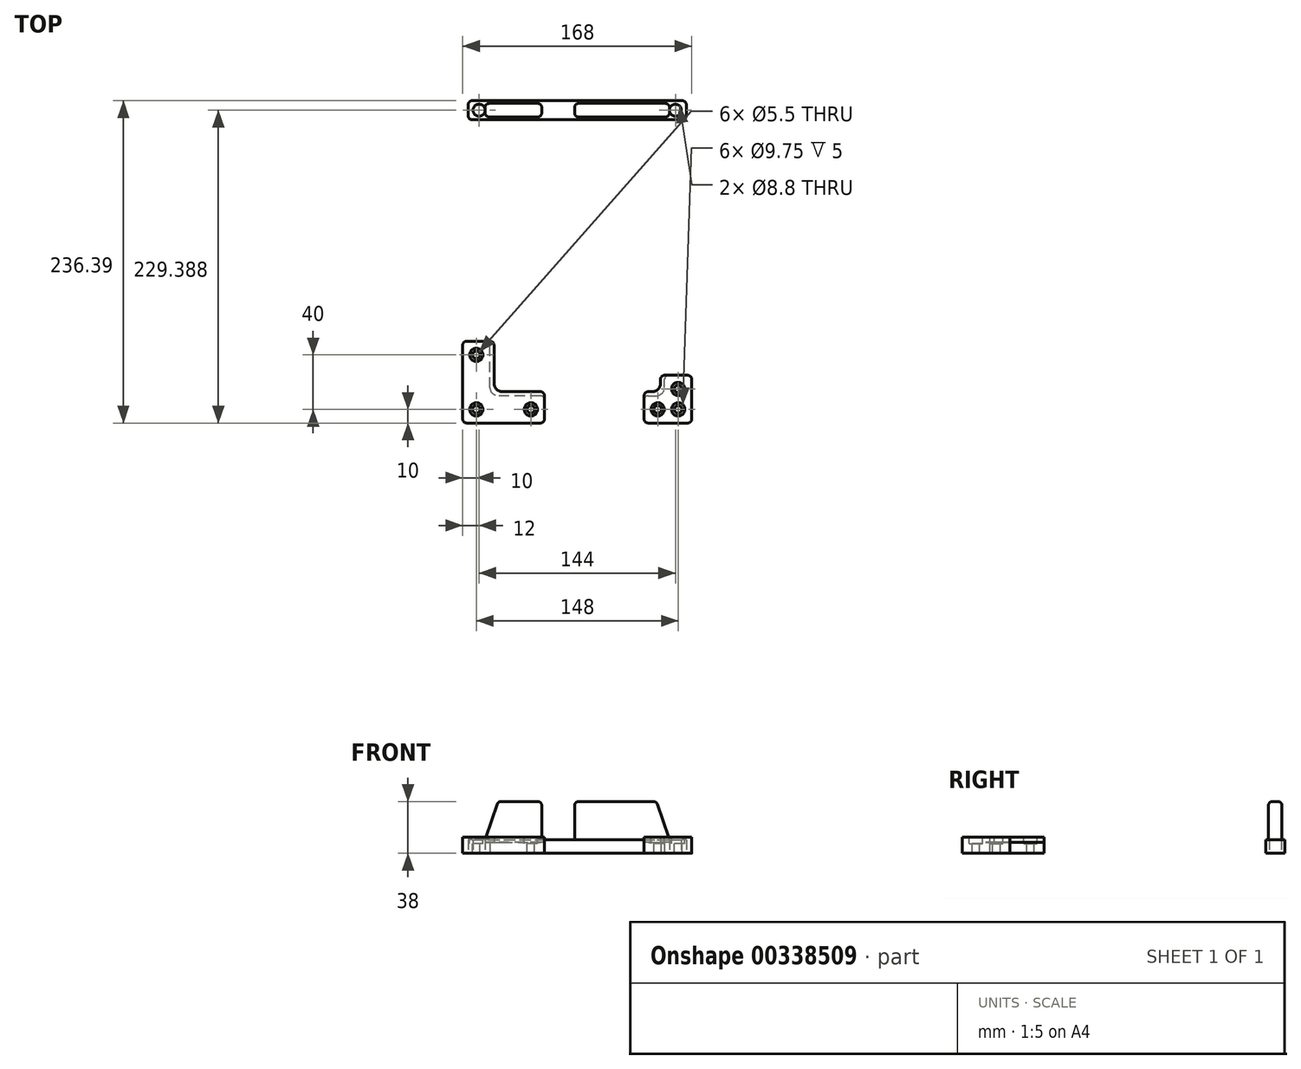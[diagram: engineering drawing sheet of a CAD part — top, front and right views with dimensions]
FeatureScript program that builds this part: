
annotation { "Feature Type Name" : "Feature", "Feature Type Description" : "" }
export const myFeature = defineFeature(function(context is Context, id is Id, definition is map)
    precondition{}
    {
        {
            var Q0;
            Q0=qCreatedBy(makeId("Top.planeOp"),FACE);
            var sketch = newSketch(context, id + "F0", { "sketchPlane" : qUnion([Q0])});
            skLineSegment(sketch, "E0.bottom", {"start": v(64, 114) * mm, "end": v(-64, 114) * mm, "construction": true});
            skLineSegment(sketch, "E0.top", {"start": v(64, -114) * mm, "end": v(-64, -114) * mm, "construction": true});
            skLineSegment(sketch, "E0.left", {"start": v(64, 114) * mm, "end": v(64, -114) * mm, "construction": true});
            skLineSegment(sketch, "E0.right", {"start": v(-64, 114) * mm, "end": v(-64, -114) * mm, "construction": true});
            skPoint(sketch, "E0.middle", {"position": v(0, 0) * mm});
            skLineSegment(sketch, "E1.bottom", {"start": v(88.4, -74) * mm, "end": v(-88.4, -74) * mm, "construction": true});
            skLineSegment(sketch, "E1.top", {"start": v(88.4, 9) * mm, "end": v(-88.4, 9) * mm, "construction": true});
            skLineSegment(sketch, "E1.left", {"start": v(88.4, -74) * mm, "end": v(88.4, 9) * mm, "construction": true});
            skLineSegment(sketch, "E1.right", {"start": v(-88.4, -74) * mm, "end": v(-88.4, 9) * mm, "construction": true});
            skPoint(sketch, "E1.middle", {"position": v(0, -32.5) * mm});
            skLineSegment(sketch, "E2", {"start": v(-64, -114) * mm, "end": v(-64, -74) * mm});
            skLineSegment(sketch, "E3", {"start": v(-64, -74) * mm, "end": v(-84, -74) * mm});
            skLineSegment(sketch, "E4", {"start": v(-84, -74) * mm, "end": v(-84, -134) * mm});
            skLineSegment(sketch, "E5", {"start": v(-84, -134) * mm, "end": v(-24, -134) * mm});
            skLineSegment(sketch, "E6", {"start": v(-24, -134) * mm, "end": v(-24, -114) * mm});
            skLineSegment(sketch, "E7", {"start": v(-24, -114) * mm, "end": v(-64, -114) * mm});
            skLineSegment(sketch, "E8", {"start": v(64, -114) * mm, "end": v(64, -99) * mm});
            skLineSegment(sketch, "E9", {"start": v(64, -99) * mm, "end": v(84, -99) * mm});
            skLineSegment(sketch, "E10", {"start": v(84, -99) * mm, "end": v(84, -134) * mm});
            skLineSegment(sketch, "E11", {"start": v(84, -134) * mm, "end": v(49, -134) * mm});
            skLineSegment(sketch, "E12", {"start": v(49, -134) * mm, "end": v(49, -114) * mm});
            skLineSegment(sketch, "E13", {"start": v(49, -114) * mm, "end": v(64, -114) * mm});
            skLineSegment(sketch, "E14.bottom", {"start": v(-80, 102.39) * mm, "end": v(80, 102.39) * mm});
            skLineSegment(sketch, "E14.top", {"start": v(-80, 88.39) * mm, "end": v(80, 88.39) * mm});
            skLineSegment(sketch, "E14.left", {"start": v(-80, 102.39) * mm, "end": v(-80, 88.39) * mm});
            skLineSegment(sketch, "E14.right", {"start": v(80, 102.39) * mm, "end": v(80, 88.39) * mm});
            skLineSegment(sketch, "E15", {"start": v(-80, 95.39) * mm, "end": v(-72, 95.39) * mm, "construction": true});
            skLineSegment(sketch, "E16", {"start": v(80, 95.39) * mm, "end": v(72, 95.39) * mm, "construction": true});
            skSolve(sketch);
        }
        {
            var Q0;
            Q0=makeQuery(id+"F0.imprint","IMPRINT",FACE,{"disambiguationData":[TD([[makeQuery(id+"F0.imprint","IMPRINT",EDGE,{"derivedFrom":sQuery(id+"F0.wireOp",EDGE,"E2")}),1.0]])]});
            var Q1;
            Q1=makeQuery(id+"F0.imprint","IMPRINT",FACE,{"disambiguationData":[TD([[makeQuery(id+"F0.imprint","IMPRINT",EDGE,{"derivedFrom":sQuery(id+"F0.wireOp",EDGE,"E8")}),-1.0]])]});
            extrude(context, id + "F1", {"entities" : qUnion([Q0, Q1]), "depth" : 8 * mm});
        }
        {
            assignVariable(context, id + "F2", {"name" : "offset", "anyValue" : 3});
        }
        {
            var Q0;
            Q0=makeQuery(id+"F1.opExtrude","CAP_FACE",FACE,{"disambiguationData":[OSD([sQuery(id+"F0.wireOp",EDGE,"E2"),sQuery(id+"F0.wireOp",EDGE,"E3"),sQuery(id+"F0.wireOp",EDGE,"E4"),sQuery(id+"F0.wireOp",EDGE,"E5"),sQuery(id+"F0.wireOp",EDGE,"E6"),sQuery(id+"F0.wireOp",EDGE,"E7")])],"isStart":false});
            var sketch = newSketch(context, id + "F3", { "sketchPlane" : qUnion([Q0])});
            skLineSegment(sketch, "E17", {"start": v(-84, -74) * mm, "end": v(-61, -74) * mm});
            skLineSegment(sketch, "E18", {"start": v(-61, -74) * mm, "end": v(-61, -111) * mm});
            skLineSegment(sketch, "E19", {"start": v(-61, -111) * mm, "end": v(-24, -111) * mm});
            skLineSegment(sketch, "E20", {"start": v(-24, -111) * mm, "end": v(-24, -134) * mm});
            skLineSegment(sketch, "E21", {"start": v(-24, -134) * mm, "end": v(-84, -134) * mm});
            skLineSegment(sketch, "E22", {"start": v(-84, -134) * mm, "end": v(-84, -74) * mm});
            skPoint(sketch, "E23.0", {"position": v(49, -134) * mm});
            skPoint(sketch, "E23.1", {"position": v(84, -134) * mm});
            skPoint(sketch, "E23.2", {"position": v(84, -99) * mm});
            skLineSegment(sketch, "E24", {"start": v(49, -134) * mm, "end": v(84, -134) * mm});
            skLineSegment(sketch, "E25", {"start": v(84, -99) * mm, "end": v(61, -99) * mm});
            skLineSegment(sketch, "E26", {"start": v(61, -99) * mm, "end": v(61, -111) * mm});
            skLineSegment(sketch, "E27", {"start": v(61, -111) * mm, "end": v(49, -111) * mm});
            skLineSegment(sketch, "E28", {"start": v(49, -111) * mm, "end": v(49, -134) * mm});
            skLineSegment(sketch, "E29", {"start": v(84, -134) * mm, "end": v(84, -99) * mm});
            skSolve(sketch);
        }
        {
            var Q0;
            {var subQ4=sQuery(id+"F3.wireOp",EDGE,"E18");Q0=makeQuery(id+"F3.imprint","IMPRINT",FACE,{"disambiguationData":[TD([[makeQuery(id+"F3.imprint","IMPRINT",EDGE,{"derivedFrom":subQ4}),-1.0]])]});}
            var Q1;
            {var subQ1=sQuery(id+"F3.wireOp",EDGE,"E21");Q1=makeQuery(id+"F3.imprint","IMPRINT",FACE,{"disambiguationData":[TD([[makeQuery(id+"F3.imprint","IMPRINT",EDGE,{"derivedFrom":subQ1}),1.0]])]});}
            var Q2;
            Q2=makeQuery(id+"F3.imprint","IMPRINT",FACE,{"disambiguationData":[TD([[makeQuery(id+"F3.imprint","IMPRINT",EDGE,{"derivedFrom":sQuery(id+"F3.wireOp",EDGE,"E24")}),1.0]])]});
            extrude(context, id + "F4", {"entities" : qUnion([Q0, Q1, Q2]), "operationType" : NewBodyOperationType.ADD, "depth" : 4 * mm});
        }
        {
            var Q0;
            Q0=makeQuery(id+"F4.boolean.opBoolean","MERGE",EDGE,{"derivedFrom":[makeQuery(id+"F1.opExtrude","SWEPT_EDGE",EDGE,{"disambiguationData":[OSD([sQuery(id+"F0.wireOp",EDGE,"E4"),sQuery(id+"F0.wireOp",EDGE,"E5")])]}),makeQuery(id+"F4.opExtrude","SWEPT_EDGE",EDGE,{"disambiguationData":[OSD([sQuery(id+"F3.wireOp",EDGE,"E21"),sQuery(id+"F3.wireOp",EDGE,"E22")])]})]});
            var Q1;
            Q1=makeQuery(id+"F4.boolean.opBoolean","MERGE",EDGE,{"derivedFrom":[makeQuery(id+"F1.opExtrude","SWEPT_EDGE",EDGE,{"disambiguationData":[OSD([sQuery(id+"F0.wireOp",EDGE,"E5"),sQuery(id+"F0.wireOp",EDGE,"E6")])]}),makeQuery(id+"F4.opExtrude","SWEPT_EDGE",EDGE,{"disambiguationData":[OSD([sQuery(id+"F3.wireOp",EDGE,"E20"),sQuery(id+"F3.wireOp",EDGE,"E21")])]})]});
            var Q2;
            Q2=makeQuery(id+"F4.boolean.opBoolean","MERGE",EDGE,{"derivedFrom":[makeQuery(id+"F1.opExtrude","SWEPT_EDGE",EDGE,{"disambiguationData":[OSD([sQuery(id+"F0.wireOp",EDGE,"E3"),sQuery(id+"F0.wireOp",EDGE,"E4")])]}),makeQuery(id+"F4.opExtrude","SWEPT_EDGE",EDGE,{"disambiguationData":[OSD([sQuery(id+"F3.wireOp",EDGE,"E17"),sQuery(id+"F3.wireOp",EDGE,"E22")])]})]});
            var Q3;
            Q3=makeQuery(id+"F4.boolean.opBoolean","MERGE",EDGE,{"derivedFrom":[makeQuery(id+"F1.opExtrude","SWEPT_EDGE",EDGE,{"disambiguationData":[OSD([sQuery(id+"F0.wireOp",EDGE,"E11"),sQuery(id+"F0.wireOp",EDGE,"E12")])]}),makeQuery(id+"F4.opExtrude","SWEPT_EDGE",EDGE,{"disambiguationData":[OSD([sQuery(id+"F3.wireOp",EDGE,"E24"),sQuery(id+"F3.wireOp",EDGE,"E28")])]})]});
            var Q4;
            Q4=makeQuery(id+"F4.boolean.opBoolean","MERGE",EDGE,{"derivedFrom":[makeQuery(id+"F1.opExtrude","SWEPT_EDGE",EDGE,{"disambiguationData":[OSD([sQuery(id+"F0.wireOp",EDGE,"E10"),sQuery(id+"F0.wireOp",EDGE,"E11")])]}),makeQuery(id+"F4.opExtrude","SWEPT_EDGE",EDGE,{"disambiguationData":[OSD([sQuery(id+"F3.wireOp",EDGE,"E24"),sQuery(id+"F3.wireOp",EDGE,"E29")])]})]});
            var Q5;
            Q5=makeQuery(id+"F4.boolean.opBoolean","MERGE",EDGE,{"derivedFrom":[makeQuery(id+"F1.opExtrude","SWEPT_EDGE",EDGE,{"disambiguationData":[OSD([sQuery(id+"F0.wireOp",EDGE,"E9"),sQuery(id+"F0.wireOp",EDGE,"E10")])]}),makeQuery(id+"F4.opExtrude","SWEPT_EDGE",EDGE,{"disambiguationData":[OSD([sQuery(id+"F3.wireOp",EDGE,"E25"),sQuery(id+"F3.wireOp",EDGE,"E29")])]})]});
            var Q6;
            Q6=makeQuery(id+"F1.opExtrude","SWEPT_EDGE",EDGE,{"disambiguationData":[OSD([sQuery(id+"F0.wireOp",EDGE,"E12"),sQuery(id+"F0.wireOp",EDGE,"E13")])]});
            var Q7;
            Q7=makeQuery(id+"F1.opExtrude","SWEPT_EDGE",EDGE,{"disambiguationData":[OSD([sQuery(id+"F0.wireOp",EDGE,"E8"),sQuery(id+"F0.wireOp",EDGE,"E9")])]});
            var Q8;
            Q8=makeQuery(id+"F1.opExtrude","SWEPT_EDGE",EDGE,{"disambiguationData":[OSD([sQuery(id+"F0.wireOp",EDGE,"E2"),sQuery(id+"F0.wireOp",EDGE,"E3")])]});
            var Q9;
            Q9=makeQuery(id+"F1.opExtrude","SWEPT_EDGE",EDGE,{"disambiguationData":[OSD([sQuery(id+"F0.wireOp",EDGE,"E6"),sQuery(id+"F0.wireOp",EDGE,"E7")])]});
            var Q10;
            Q10=makeQuery(id+"F4.opExtrude","SWEPT_EDGE",EDGE,{"disambiguationData":[OSD([sQuery(id+"F3.wireOp",EDGE,"E27"),sQuery(id+"F3.wireOp",EDGE,"E28")])]});
            var Q11;
            Q11=makeQuery(id+"F4.opExtrude","SWEPT_EDGE",EDGE,{"disambiguationData":[OSD([sQuery(id+"F3.wireOp",EDGE,"E25"),sQuery(id+"F3.wireOp",EDGE,"E26")])]});
            var Q12;
            Q12=makeQuery(id+"F4.opExtrude","SWEPT_EDGE",EDGE,{"disambiguationData":[OSD([sQuery(id+"F3.wireOp",EDGE,"E17"),sQuery(id+"F3.wireOp",EDGE,"E18")])]});
            var Q13;
            Q13=makeQuery(id+"F4.opExtrude","SWEPT_EDGE",EDGE,{"disambiguationData":[OSD([sQuery(id+"F3.wireOp",EDGE,"E19"),sQuery(id+"F3.wireOp",EDGE,"E20")])]});
            fillet(context, id + "F5", {"entities" : qUnion([Q0, Q1, Q2, Q3, Q4, Q5, Q6, Q7, Q8, Q9, Q10, Q11, Q12, Q13]), "radius" : (getVariable(context, 'offset')) * mm, "tangentPropagation" : true, "allowEdgeOverflow" : false});
        }
        {
            var Q0;
            Q0=makeQuery(id+"F1.opExtrude","SWEPT_EDGE",EDGE,{"disambiguationData":[OSD([sQuery(id+"F0.wireOp",EDGE,"E8"),sQuery(id+"F0.wireOp",EDGE,"E13")])]});
            var Q1;
            Q1=makeQuery(id+"F4.opExtrude","SWEPT_EDGE",EDGE,{"disambiguationData":[OSD([sQuery(id+"F3.wireOp",EDGE,"E26"),sQuery(id+"F3.wireOp",EDGE,"E27")])]});
            var Q2;
            Q2=makeQuery(id+"F1.opExtrude","SWEPT_EDGE",EDGE,{"disambiguationData":[OSD([sQuery(id+"F0.wireOp",EDGE,"E2"),sQuery(id+"F0.wireOp",EDGE,"E7")])]});
            var Q3;
            Q3=makeQuery(id+"F4.opExtrude","SWEPT_EDGE",EDGE,{"disambiguationData":[OSD([sQuery(id+"F3.wireOp",EDGE,"E18"),sQuery(id+"F3.wireOp",EDGE,"E19")])]});
            fillet(context, id + "F6", {"entities" : qUnion([Q0, Q1, Q2, Q3]), "radius" : 6 * mm, "tangentPropagation" : true, "allowEdgeOverflow" : false});
        }
        {
            var Q0;
            Q0=makeQuery(id+"F4.opExtrude","CAP_FACE",FACE,{"disambiguationData":[OSD([sQuery(id+"F3.wireOp",EDGE,"E17"),sQuery(id+"F3.wireOp",EDGE,"E18"),sQuery(id+"F3.wireOp",EDGE,"E19"),sQuery(id+"F3.wireOp",EDGE,"E20"),sQuery(id+"F3.wireOp",EDGE,"E21"),sQuery(id+"F3.wireOp",EDGE,"E22")])],"isStart":false});
            var sketch = newSketch(context, id + "F7", { "sketchPlane" : qUnion([Q0])});
            skLineSegment(sketch, "E30.0.0", {"start": v(61, -102) * mm, "end": v(61, -105) * mm, "construction": true});
            skArc(sketch, "E30.0.1", {"start": v(61, -105) * mm, "mid": v(59.24, -109.24) * mm, "end": v(55, -111) * mm, "construction": true});
            skLineSegment(sketch, "E30.0.2", {"start": v(55, -111) * mm, "end": v(52, -111) * mm, "construction": true});
            skArc(sketch, "E30.0.3", {"start": v(52, -111) * mm, "mid": v(49.88, -111.88) * mm, "end": v(49, -114) * mm, "construction": true});
            skLineSegment(sketch, "E30.0.4", {"start": v(49, -114) * mm, "end": v(49, -131) * mm, "construction": true});
            skArc(sketch, "E30.0.5", {"start": v(49, -131) * mm, "mid": v(49.88, -133.12) * mm, "end": v(52, -134) * mm, "construction": true});
            skLineSegment(sketch, "E30.0.6", {"start": v(52, -134) * mm, "end": v(81, -134) * mm, "construction": true});
            skArc(sketch, "E30.0.7", {"start": v(81, -134) * mm, "mid": v(83.12, -133.12) * mm, "end": v(84, -131) * mm, "construction": true});
            skLineSegment(sketch, "E30.0.8", {"start": v(84, -131) * mm, "end": v(84, -102) * mm, "construction": true});
            skArc(sketch, "E30.0.9", {"start": v(84, -102) * mm, "mid": v(83.12, -99.88) * mm, "end": v(81, -99) * mm, "construction": true});
            skLineSegment(sketch, "E30.0.10", {"start": v(81, -99) * mm, "end": v(64, -99) * mm, "construction": true});
            skArc(sketch, "E30.0.11", {"start": v(64, -99) * mm, "mid": v(61.88, -99.88) * mm, "end": v(61, -102) * mm, "construction": true});
            skPoint(sketch, "E31.0", {"position": v(-84, -134) * mm});
            skPoint(sketch, "E31.1", {"position": v(-24, -134) * mm});
            skPoint(sketch, "E31.2", {"position": v(49, -134) * mm});
            skPoint(sketch, "E31.3", {"position": v(84, -134) * mm});
            skPoint(sketch, "E31.4", {"position": v(84, -99) * mm});
            skPoint(sketch, "E31.5", {"position": v(-84, -74) * mm});
            skLineSegment(sketch, "E32", {"start": v(-84, -74) * mm, "end": v(-74, -74) * mm, "construction": true});
            skLineSegment(sketch, "E33", {"start": v(-74, -74) * mm, "end": v(-74, -124) * mm, "construction": true});
            skLineSegment(sketch, "E34", {"start": v(-74, -124) * mm, "end": v(-24, -124) * mm, "construction": true});
            skLineSegment(sketch, "E35", {"start": v(49, -124) * mm, "end": v(74, -124) * mm, "construction": true});
            skLineSegment(sketch, "E36", {"start": v(74, -124) * mm, "end": v(74, -99) * mm, "construction": true});
            skPoint(sketch, "E37", {"position": v(-74, -84) * mm});
            skPoint(sketch, "E38", {"position": v(-34, -124) * mm});
            skPoint(sketch, "E39", {"position": v(59, -124) * mm});
            skPoint(sketch, "E40", {"position": v(74, -109) * mm});
            skPoint(sketch, "E41", {"position": v(-74, -124) * mm});
            skPoint(sketch, "E42", {"position": v(74, -124) * mm});
            skSolve(sketch);
        }
        {
            var Q0;
            Q0=sQuery(id+"F7.wireOp",VERTEX,"E41");
            var Q1;
            Q1=sQuery(id+"F7.wireOp",VERTEX,"E37");
            var Q2;
            Q2=sQuery(id+"F7.wireOp",VERTEX,"E38");
            var Q3;
            Q3=sQuery(id+"F7.wireOp",VERTEX,"E39");
            var Q4;
            Q4=sQuery(id+"F7.wireOp",VERTEX,"E42");
            var Q5;
            Q5=sQuery(id+"F7.wireOp",VERTEX,"E40");
            var Q6;
            Q6=makeQuery(id+"F1.opExtrude","SWEPT_BODY",BODY,{"disambiguationData":[OSD([sQuery(id+"F0.wireOp",EDGE,"E2"),sQuery(id+"F0.wireOp",EDGE,"E3"),sQuery(id+"F0.wireOp",EDGE,"E4"),sQuery(id+"F0.wireOp",EDGE,"E5"),sQuery(id+"F0.wireOp",EDGE,"E6"),sQuery(id+"F0.wireOp",EDGE,"E7")])]});
            var Q7;
            Q7=makeQuery(id+"F1.opExtrude","SWEPT_BODY",BODY,{"disambiguationData":[OSD([sQuery(id+"F0.wireOp",EDGE,"E8"),sQuery(id+"F0.wireOp",EDGE,"E9"),sQuery(id+"F0.wireOp",EDGE,"E10"),sQuery(id+"F0.wireOp",EDGE,"E11"),sQuery(id+"F0.wireOp",EDGE,"E12"),sQuery(id+"F0.wireOp",EDGE,"E13")])]});
            hole(context, id + "F8", {"style" : HoleStyle.C_BORE, "endStyle" : HoleEndStyle.BLIND, "standardTappedOrClearance" : lookupTablePath({ "standard" : "ISO", "fit" : "Normal", "size" : "M5", "type" : "Clearance" }), "standardBlindInLast" : lookupTablePath({ "fit" : "Standard", "standard" : "ISO", "size" : "M5", "type" : "Clearance" }), "holeDiameter" : 5.5 * mm, "cBoreDiameter" : 9.75 * mm, "cBoreDepth" : 5 * mm, "holeDepth" : 40 * mm, "tappedDepth" : 12 * mm, "tapClearance" : 3, "locations" : qUnion([Q0, Q1, Q2, Q3, Q4, Q5]), "scope" : qUnion([Q6, Q7])});
        }
        {
            var Q0;
            Q0=makeQuery(id+"F0.imprint","IMPRINT",FACE,{"disambiguationData":[TD([[makeQuery(id+"F0.imprint","IMPRINT",EDGE,{"derivedFrom":sQuery(id+"F0.wireOp",EDGE,"E14.bottom")}),-1.0]])]});
            extrude(context, id + "F9", {"entities" : qUnion([Q0]), "depth" : 10 * mm});
        }
        {
            var Q0;
            Q0=makeQuery(id+"F9.opExtrude","CAP_FACE",FACE,{"disambiguationData":[OSD([sQuery(id+"F0.wireOp",EDGE,"E14.bottom"),sQuery(id+"F0.wireOp",EDGE,"E14.top"),sQuery(id+"F0.wireOp",EDGE,"E14.left"),sQuery(id+"F0.wireOp",EDGE,"E14.right")])],"isStart":false});
            var sketch = newSketch(context, id + "F10", { "sketchPlane" : qUnion([Q0])});
            skLineSegment(sketch, "E43.bottom", {"start": v(-58, 90.39) * mm, "end": v(-26, 90.39) * mm});
            skLineSegment(sketch, "E43.top", {"start": v(-58, 100.39) * mm, "end": v(-26, 100.39) * mm});
            skLineSegment(sketch, "E43.left", {"start": v(-58, 90.39) * mm, "end": v(-58, 100.39) * mm});
            skLineSegment(sketch, "E43.right", {"start": v(-26, 90.39) * mm, "end": v(-26, 100.39) * mm});
            skLineSegment(sketch, "E44.bottom", {"start": v(-2, 90.39) * mm, "end": v(58, 90.39) * mm});
            skLineSegment(sketch, "E44.top", {"start": v(-2, 100.39) * mm, "end": v(58, 100.39) * mm});
            skLineSegment(sketch, "E44.left", {"start": v(-2, 90.39) * mm, "end": v(-2, 100.39) * mm});
            skLineSegment(sketch, "E44.right", {"start": v(58, 90.39) * mm, "end": v(58, 100.39) * mm});
            skSolve(sketch);
        }
        {
            var Q0;
            Q0=makeQuery(id+"F10.imprint","IMPRINT",FACE,{"disambiguationData":[TD([[makeQuery(id+"F10.imprint","IMPRINT",EDGE,{"derivedFrom":sQuery(id+"F10.wireOp",EDGE,"E43.bottom")}),1.0]])]});
            var Q1;
            Q1=makeQuery(id+"F10.imprint","IMPRINT",FACE,{"disambiguationData":[TD([[makeQuery(id+"F10.imprint","IMPRINT",EDGE,{"derivedFrom":sQuery(id+"F10.wireOp",EDGE,"E44.bottom")}),1.0]])]});
            extrude(context, id + "F11", {"entities" : qUnion([Q0, Q1]), "operationType" : NewBodyOperationType.ADD, "depth" : 28 * mm});
        }
        {
            var Q0;
            Q0=sQuery(id+"F0.wireOp",VERTEX,"E15.end");
            var Q1;
            Q1=sQuery(id+"F0.wireOp",VERTEX,"E16.end");
            var Q2;
            Q2=makeQuery(id+"F9.opExtrude","SWEPT_BODY",BODY,{"disambiguationData":[OSD([sQuery(id+"F0.wireOp",EDGE,"E14.bottom"),sQuery(id+"F0.wireOp",EDGE,"E14.top"),sQuery(id+"F0.wireOp",EDGE,"E14.left"),sQuery(id+"F0.wireOp",EDGE,"E14.right")])]});
            hole(context, id + "F12", {"style" : HoleStyle.SIMPLE, "endStyle" : HoleEndStyle.BLIND, "oppositeDirection" : true, "standardTappedOrClearance" : lookupTablePath({ "standard" : "ISO", "fit" : "Normal", "size" : "M8", "type" : "Clearance" }), "standardBlindInLast" : lookupTablePath({ "fit" : "Standard", "standard" : "ISO", "size" : "M8", "type" : "Clearance" }), "holeDiameter" : 8.8 * mm, "holeDepth" : 15.75 * mm, "tappedDepth" : 12 * mm, "tapClearance" : 3, "locations" : qUnion([Q0, Q1]), "scope" : qUnion([Q2])});
        }
        {
            var Q0;
            Q0=makeQuery(id+"F11.opExtrude","SWEPT_FACE",FACE,{"disambiguationData":[OSD([sQuery(id+"F10.wireOp",EDGE,"E43.bottom")])]});
            var sketch = newSketch(context, id + "F13", { "sketchPlane" : qUnion([Q0])});
            skPoint(sketch, "E45.0", {"position": v(58, 10) * mm});
            skPoint(sketch, "E46.0", {"position": v(58, 38) * mm});
            skPoint(sketch, "E47.0", {"position": v(-58, 38) * mm});
            skPoint(sketch, "E48.0", {"position": v(-58, 10) * mm});
            skLineSegment(sketch, "E49.0", {"start": v(-67.6, 10) * mm, "end": v(-76.4, 10) * mm, "construction": true});
            skLineSegment(sketch, "E50", {"start": v(67.6, 0) * mm, "end": v(67.6, 10) * mm, "construction": true});
            skLineSegment(sketch, "E51", {"start": v(-67.6, 10) * mm, "end": v(-58, 10) * mm});
            skLineSegment(sketch, "E52", {"start": v(-58, 38) * mm, "end": v(-67.6, 10) * mm});
            skLineSegment(sketch, "E53", {"start": v(67.6, 10) * mm, "end": v(58, 10) * mm});
            skLineSegment(sketch, "E54", {"start": v(58, 38) * mm, "end": v(67.6, 10) * mm});
            skLineSegment(sketch, "E55", {"start": v(58, 38) * mm, "end": v(58, 10) * mm});
            skSolve(sketch);
        }
        {
            var Q0;
            Q0=makeQuery(id+"F13.imprint","IMPRINT",FACE,{"disambiguationData":[TD([[makeQuery(id+"F13.imprint","IMPRINT",EDGE,{"derivedFrom":sQuery(id+"F13.wireOp",EDGE,"E51")}),1.0]])]});
            var Q1;
            Q1=makeQuery(id+"F13.imprint","IMPRINT",FACE,{"disambiguationData":[TD([[makeQuery(id+"F13.imprint","IMPRINT",EDGE,{"derivedFrom":sQuery(id+"F13.wireOp",EDGE,"E53")}),-1.0]])]});
            var Q2;
            Q2=makeQuery(id+"F11.opExtrude","SWEPT_FACE",FACE,{"disambiguationData":[OSD([sQuery(id+"F10.wireOp",EDGE,"E43.top")])]});
            extrude(context, id + "F14", {"entities" : qUnion([Q0, Q1]), "operationType" : NewBodyOperationType.ADD, "endBound" : BoundingType.UP_TO_SURFACE, "oppositeDirection" : true, "endBoundEntityFace" : qUnion([Q2]), "depth" : 25 * mm});
        }
        {
            var Q0;
            Q0=makeQuery(id+"F9.opExtrude","SWEPT_EDGE",EDGE,{"disambiguationData":[OSD([sQuery(id+"F0.wireOp",EDGE,"E14.top"),sQuery(id+"F0.wireOp",EDGE,"E14.left")])]});
            var Q1;
            Q1=makeQuery(id+"F9.opExtrude","SWEPT_EDGE",EDGE,{"disambiguationData":[OSD([sQuery(id+"F0.wireOp",EDGE,"E14.bottom"),sQuery(id+"F0.wireOp",EDGE,"E14.left")])]});
            var Q2;
            Q2=makeQuery(id+"F9.opExtrude","SWEPT_EDGE",EDGE,{"disambiguationData":[OSD([sQuery(id+"F0.wireOp",EDGE,"E14.top"),sQuery(id+"F0.wireOp",EDGE,"E14.right")])]});
            var Q3;
            Q3=makeQuery(id+"F9.opExtrude","SWEPT_EDGE",EDGE,{"disambiguationData":[OSD([sQuery(id+"F0.wireOp",EDGE,"E14.bottom"),sQuery(id+"F0.wireOp",EDGE,"E14.right")])]});
            var Q4;
            Q4=makeQuery(id+"F14.opExtrude","CAP_EDGE",EDGE,{"disambiguationData":[OSD([sQuery(id+"F13.wireOp",EDGE,"E54")])],"isStart":false});
            var Q5;
            Q5=makeQuery(id+"F14.opExtrude","CAP_EDGE",EDGE,{"disambiguationData":[OSD([sQuery(id+"F13.wireOp",EDGE,"E54")])],"isStart":true});
            var Q6;
            Q6=makeQuery(id+"F14.opExtrude","CAP_EDGE",EDGE,{"disambiguationData":[OSD([sQuery(id+"F13.wireOp",EDGE,"E52")])],"isStart":false});
            var Q7;
            Q7=makeQuery(id+"F14.opExtrude","CAP_EDGE",EDGE,{"disambiguationData":[OSD([sQuery(id+"F13.wireOp",EDGE,"E52")])],"isStart":true});
            var Q8;
            Q8=makeQuery(id+"F11.opExtrude","SWEPT_EDGE",EDGE,{"disambiguationData":[OSD([sQuery(id+"F10.wireOp",EDGE,"E44.top"),sQuery(id+"F10.wireOp",EDGE,"E44.left")])]});
            var Q9;
            Q9=makeQuery(id+"F11.opExtrude","SWEPT_EDGE",EDGE,{"disambiguationData":[OSD([sQuery(id+"F10.wireOp",EDGE,"E44.bottom"),sQuery(id+"F10.wireOp",EDGE,"E44.left")])]});
            var Q10;
            Q10=makeQuery(id+"F11.opExtrude","SWEPT_EDGE",EDGE,{"disambiguationData":[OSD([sQuery(id+"F10.wireOp",EDGE,"E43.bottom"),sQuery(id+"F10.wireOp",EDGE,"E43.right")])]});
            var Q11;
            Q11=makeQuery(id+"F11.opExtrude","SWEPT_EDGE",EDGE,{"disambiguationData":[OSD([sQuery(id+"F10.wireOp",EDGE,"E43.top"),sQuery(id+"F10.wireOp",EDGE,"E43.right")])]});
            var Q12;
            Q12=makeQuery(id+"F11.opExtrude","CAP_EDGE",EDGE,{"disambiguationData":[OSD([sQuery(id+"F10.wireOp",EDGE,"E43.top")])],"isStart":false});
            var Q13;
            Q13=makeQuery(id+"F11.opExtrude","CAP_EDGE",EDGE,{"disambiguationData":[OSD([sQuery(id+"F10.wireOp",EDGE,"E43.bottom")])],"isStart":false});
            var Q14;
            Q14=makeQuery(id+"F11.opExtrude","CAP_EDGE",EDGE,{"disambiguationData":[OSD([sQuery(id+"F10.wireOp",EDGE,"E44.bottom")])],"isStart":false});
            var Q15;
            Q15=makeQuery(id+"F11.opExtrude","CAP_EDGE",EDGE,{"disambiguationData":[OSD([sQuery(id+"F10.wireOp",EDGE,"E44.top")])],"isStart":false});
            var Q16;
            Q16=makeQuery(id+"F11.opExtrude","CAP_EDGE",EDGE,{"disambiguationData":[OSD([sQuery(id+"F10.wireOp",EDGE,"E44.left")])],"isStart":false});
            var Q17;
            Q17=makeQuery(id+"F11.opExtrude","CAP_EDGE",EDGE,{"disambiguationData":[OSD([sQuery(id+"F10.wireOp",EDGE,"E43.right")])],"isStart":false});
            var Q18;
            {var subQ0=sQuery(id+"F10.wireOp",EDGE,"E43.left");Q18=makeQuery(id+"F14.boolean.opBoolean","MERGE",EDGE,{"derivedFrom":[makeQuery(id+"F11.opExtrude","CAP_EDGE",EDGE,{"disambiguationData":[OSD([subQ0])],"isStart":false}),makeQuery(id+"F14.opExtrude","SWEPT_EDGE",EDGE,{"disambiguationData":[OSD([sQuery(id+"F10.wireOp",EDGE,"E43.bottom"),subQ0,sQuery(id+"F13.wireOp",EDGE,"E52")])]})]});}
            var Q19;
            Q19=makeQuery(id+"F14.boolean.opBoolean","MERGE",EDGE,{"derivedFrom":[makeQuery(id+"F11.opExtrude","CAP_EDGE",EDGE,{"disambiguationData":[OSD([sQuery(id+"F10.wireOp",EDGE,"E44.right")])],"isStart":false}),makeQuery(id+"F14.opExtrude","SWEPT_EDGE",EDGE,{"disambiguationData":[OSD([sQuery(id+"F13.wireOp",EDGE,"E54"),sQuery(id+"F13.wireOp",EDGE,"E55")])]})]});
            fillet(context, id + "F15", {"entities" : qUnion([Q0, Q1, Q2, Q3, Q4, Q5, Q6, Q7, Q8, Q9, Q10, Q11, Q12, Q13, Q14, Q15, Q16, Q17, Q18, Q19]), "radius" : 3 * mm, "tangentPropagation" : true, "allowEdgeOverflow" : false});
        }
    });
